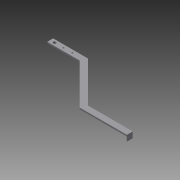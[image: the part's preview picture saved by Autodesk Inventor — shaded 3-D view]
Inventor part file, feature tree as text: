
AUTODESK INVENTOR PART (.ipt)
format: ipt  version: 2013 (Build 170138000, 138)  size: 166,400 bytes
history: native  units: in
note: dims shown in document units (in); Inventor stores cm internally (conversion verified against a paired STEP export)
features: extrude x8, sketch x8
ambient origin geometry x8: Origin, YZ Plane, XZ Plane, XY Plane, X Axis, Y Axis, Z Axis, Center Point
bodies: Solid1 (feature_tree)
feature tree (16):
  extrude  "Extrusion1"  Depth=1.0in
  extrude  "Extrusion2"  Depth=1.0in
  extrude  "Extrusion3"  Depth=9.336in
  extrude  "Extrusion5"  Depth=7.5in
  extrude  "Extrusion7"  Depth=0.25in TaperAngle=0.0deg
  extrude  "Extrusion8"  Depth=1.0in
  extrude  "Extrusion9"  Depth=1.75in TaperAngle=0.0deg
  extrude  "Extrusion10"  Depth=2.25in
  sketch  "Sketch1"  dims[d0=5.25in d1=1.0in]
  sketch  "Sketch2"  dims[d2=112.5deg d3=1.0in]
  sketch  "Sketch3"  dims[d4=135.0deg d5=9.336in]
  sketch  "Sketch6"  dims[d6=0.5in d7=7.5in]
  sketch  "Sketch8"  dims[d8=1.0in d9=0.25in d10=0.0in]
  sketch  "Sketch9"  dims[d11=1.0in d12=1.0in]
  sketch  "Sketch10"  dims[d13=0.0625in d14=0.0in d15=1.75in d16=0.0in]
  sketch  "Sketch11"  dims[d21=0.25in d22=0.0in d29=2.25in d30=1.5in d31=3.0in d32=0.0in d33=0.25in d34=0.25in d35=1.0in d36=0.0in d37=1.75in d38=1.0in d39=1.5in d40=0.0in d41=0.25in d42=1.0in d43=0.0in d44=0.25in d45=0.0in d46=0.25in d47=180.0deg d48=0.25in d49=0.0in]
